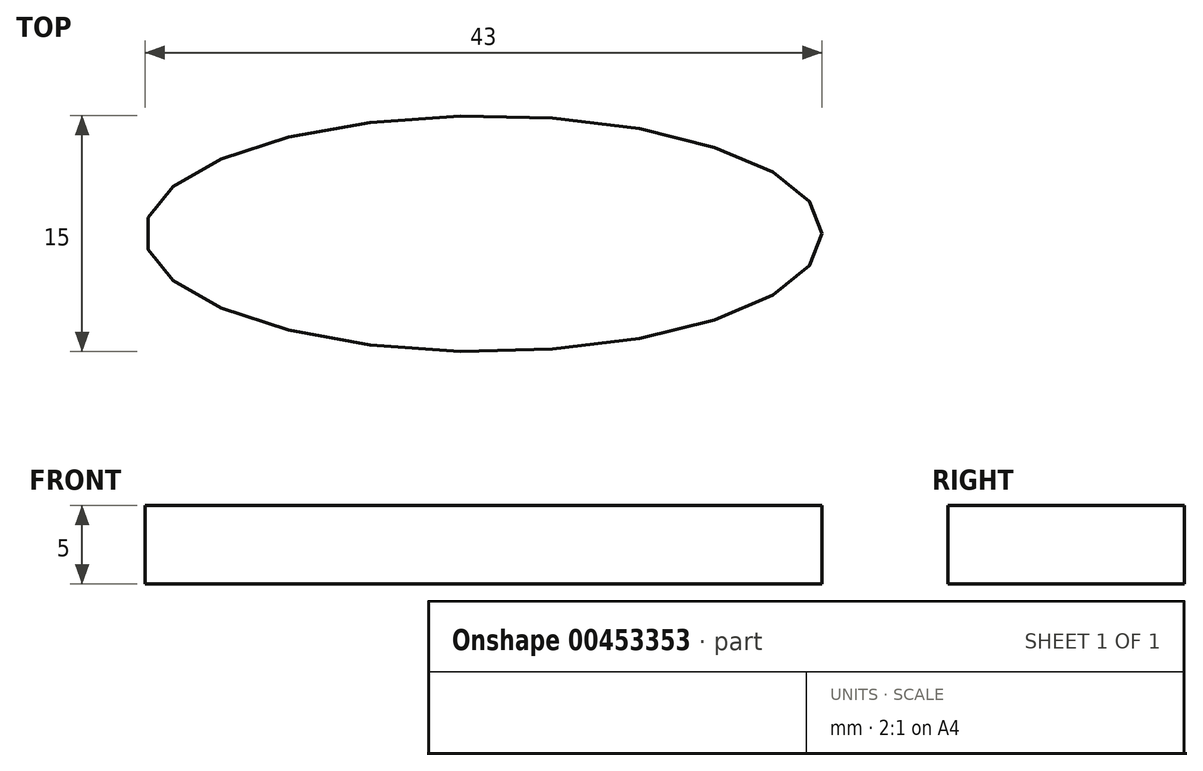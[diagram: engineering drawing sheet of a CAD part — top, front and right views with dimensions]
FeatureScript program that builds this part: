
annotation { "Feature Type Name" : "Feature", "Feature Type Description" : "" }
export const myFeature = defineFeature(function(context is Context, id is Id, definition is map)
    precondition{}
    {
        {
            var Q0;
            Q0=qCreatedBy(makeId("Top.planeOp"),FACE);
            var sketch = newSketch(context, id + "F0", { "sketchPlane" : qUnion([Q0])});
            skEllipse(sketch, "E0", {"center": v(1.65, -1.55) * mm, "majorRadius": 21.5 * mm, "minorRadius": 7.5 * mm, "majorAxis": v(1, 0)});
            skFitSpline(sketch, "E1.0", {"points": [v(22.1, -2) * mm, v(22.17, -1.55) * mm, v(22.1, -1.1) * mm, v(21.9, -0.59) * mm, v(21.5, -0.03) * mm, v(20.9, 0.55) * mm, v(20.1, 1.15) * mm, v(18.76, 1.93) * mm, v(16.63, 2.84) * mm, v(13.99, 3.6) * mm, v(11.62, 4.1) * mm, v(9.12, 4.5) * mm, v(6.47, 4.79) * mm, v(3.74, 4.93) * mm, v(1.65, 4.96) * mm, v(-0.43, 4.93) * mm, v(-3.17, 4.79) * mm, v(-5.82, 4.5) * mm, v(-8.31, 4.1) * mm, v(-10.69, 3.6) * mm, v(-13.32, 2.84) * mm, v(-15.45, 1.93) * mm, v(-16.8, 1.15) * mm, v(-17.6, 0.55) * mm, v(-18.2, -0.03) * mm, v(-18.6, -0.59) * mm, v(-18.8, -1.1) * mm, v(-18.87, -1.55) * mm, v(-18.8, -2) * mm, v(-18.6, -2.5) * mm, v(-18.2, -3.06) * mm, v(-17.6, -3.65) * mm, v(-16.8, -4.25) * mm, v(-15.45, -5.03) * mm, v(-13.32, -5.94) * mm, v(-10.69, -6.7) * mm, v(-8.31, -7.2) * mm, v(-5.82, -7.6) * mm, v(-3.17, -7.88) * mm, v(-0.43, -8.02) * mm, v(1.65, -8.06) * mm, v(3.74, -8.02) * mm, v(6.47, -7.88) * mm, v(9.12, -7.6) * mm, v(11.62, -7.2) * mm, v(13.99, -6.7) * mm, v(16.63, -5.94) * mm, v(18.76, -5.03) * mm, v(20.1, -4.25) * mm, v(20.9, -3.65) * mm, v(21.5, -3.06) * mm, v(21.9, -2.5) * mm, v(22.1, -2) * mm, v(22.17, -1.55) * mm, v(22.1, -1.1) * mm, v(22.1, -2) * mm]});
            skSolve(sketch);
        }
        {
            var Q0;
            Q0 = qSketchRegion(id + "F0", true);
            extrude(context, id + "F1", {"entities" : qUnion([Q0]), "depth" : 5 * mm});
        }
    });
